# Revit family: LAMP 400-1000 Water Heater
name_source: partatom
category: Mechanical Equipment
units: mm (PartAtom-declared; Revit-internal decimal feet)

## family parameters
Always vertical = Yes
Cut with Voids When Loaded = No
OmniClass Number = 23.75.00.00
OmniClass Title = Climate Control (HVAC)
Part Type = Normal
Room Calculation Point = No
Round Connector Dimension = Use Diameter
Shared = No
Work Plane-Based = No

## types (5) — shared parameters
Air Supply X = 5 13/16"
Air Supply Y = 12 5/16"
Boiler Drain = 3/4" NPT Female
Condensate Trap = 1" Pipe
Height = 38 17/32"
Hydronic Return = 2" NPT Male
Hydronic Supply = 2" NPT Female
Manufacturer = Bryan Steam
Vent X = 16 1/8"
Width = 26 1/8"

## per-type parameters (varying)
| type | Air Supply | Air Supply I.D. | Air Supply Length | Air Supply O.D. | Gas Train | Gas Train Ball Valve Dia. | Gas Train Ball Valve X | Gas Train Ball Valve Y | Gas Train Dia. | Gas Train X | Gas Train Y | Length | Vent | Vent I.D. | Vent Length | Vent O.D. | Vent Y |
| Little Amp/Bfit 500 Water Heater | 4" | 4 17/32" | 2 17/32" | 5 1/16" | 3/4" NPT Female | 1 1/2" | 22 27/32" | 27 17/32" | 1 1/16" | 22 27/32" | 27 17/32" | 36 5/16" | 4" | 4 9/16" | 5 9/16" | 4 31/32" | 19 23/32" |
| Little Amp/Bfit 400 Water Heater | 4" | 4 17/32" | 2 17/32" | 5 1/16" | 3/4" NPT Female | 1 1/2" | 23 1/4" | 27 13/16" | 1 1/16" | 23 1/4" | 27 13/16" | 36 5/16" | 4" | 4 9/16" | 5 9/16" | 4 31/32" | 19 23/32" |
| Little Amp/Bfit 650 Water Heater | 6" | 5 19/32" | 1 7/16" | 5 7/8" | 1" NPT Female | 1 25/32" | 22 25/32" | 27 3/32" | 1 5/16" | 22 25/32" | 27 3/32" | 52 1/8" | 6" | 6 11/16" | 7 3/32" | 7 1/8" | 19 13/16" |
| Little Amp/Bfit 800 Water Heater | 6" | 5 19/32" | 1 7/16" | 5 7/8" | 1" NPT Female | 1 25/32" | 22 27/32" | 27 5/8" | 1 5/16" | 22 27/32" | 27 5/8" | 52 1/8" | 6" | 6 11/16" | 7 3/32" | 7 1/8" | 19 13/16" |
| Little Amp/Bfit 1000 Water Heater | 6" | 5 19/32" | 1 7/16" | 5 7/8" | 1" NPT Female | 1 25/32" | 22 27/32" | 27 5/8" | 1 5/16" | 22 27/32" | 27 5/8" | 52 1/8" | 6" | 6 11/16" | 7 3/32" | 7 1/8" | 19 13/16" |

## geometry (parser evidence)
native form markers: Sweep x2
no freeform markers — native parametric forms only
